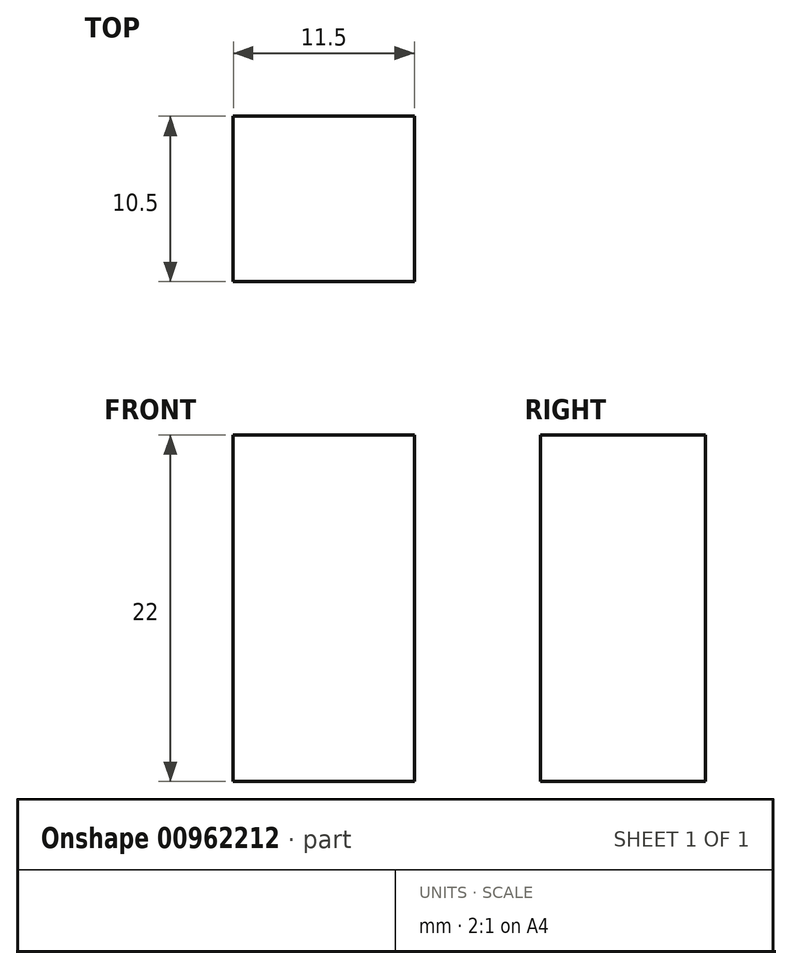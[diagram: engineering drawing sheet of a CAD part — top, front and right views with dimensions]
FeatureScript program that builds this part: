
annotation { "Feature Type Name" : "Feature", "Feature Type Description" : "" }
export const myFeature = defineFeature(function(context is Context, id is Id, definition is map)
    precondition{}
    {
        {
            var Q0;
            Q0=qCreatedBy(makeId("Top.planeOp"),FACE);
            var sketch = newSketch(context, id + "F0", { "sketchPlane" : qUnion([Q0])});
            skLineSegment(sketch, "E0.bottom", {"start": v(-5.27, 6.2) * mm, "end": v(6.23, 6.2) * mm});
            skLineSegment(sketch, "E0.top", {"start": v(-5.27, -4.3) * mm, "end": v(6.23, -4.3) * mm});
            skLineSegment(sketch, "E0.left", {"start": v(-5.27, 6.2) * mm, "end": v(-5.27, -4.3) * mm});
            skLineSegment(sketch, "E0.right", {"start": v(6.23, 6.2) * mm, "end": v(6.23, -4.3) * mm});
            skSolve(sketch);
        }
        {
            var Q0;
            Q0=makeQuery(id+"F0.imprint","IMPRINT",FACE,{"disambiguationData":[TD([[makeQuery(id+"F0.imprint","IMPRINT",EDGE,{"derivedFrom":sQuery(id+"F0.wireOp",EDGE,"E0.bottom")}),-1.0]])]});
            extrude(context, id + "F1", {"entities" : qUnion([Q0]), "depth" : 22 * mm, "offsetDistance" : 25 * mm});
        }
    });
